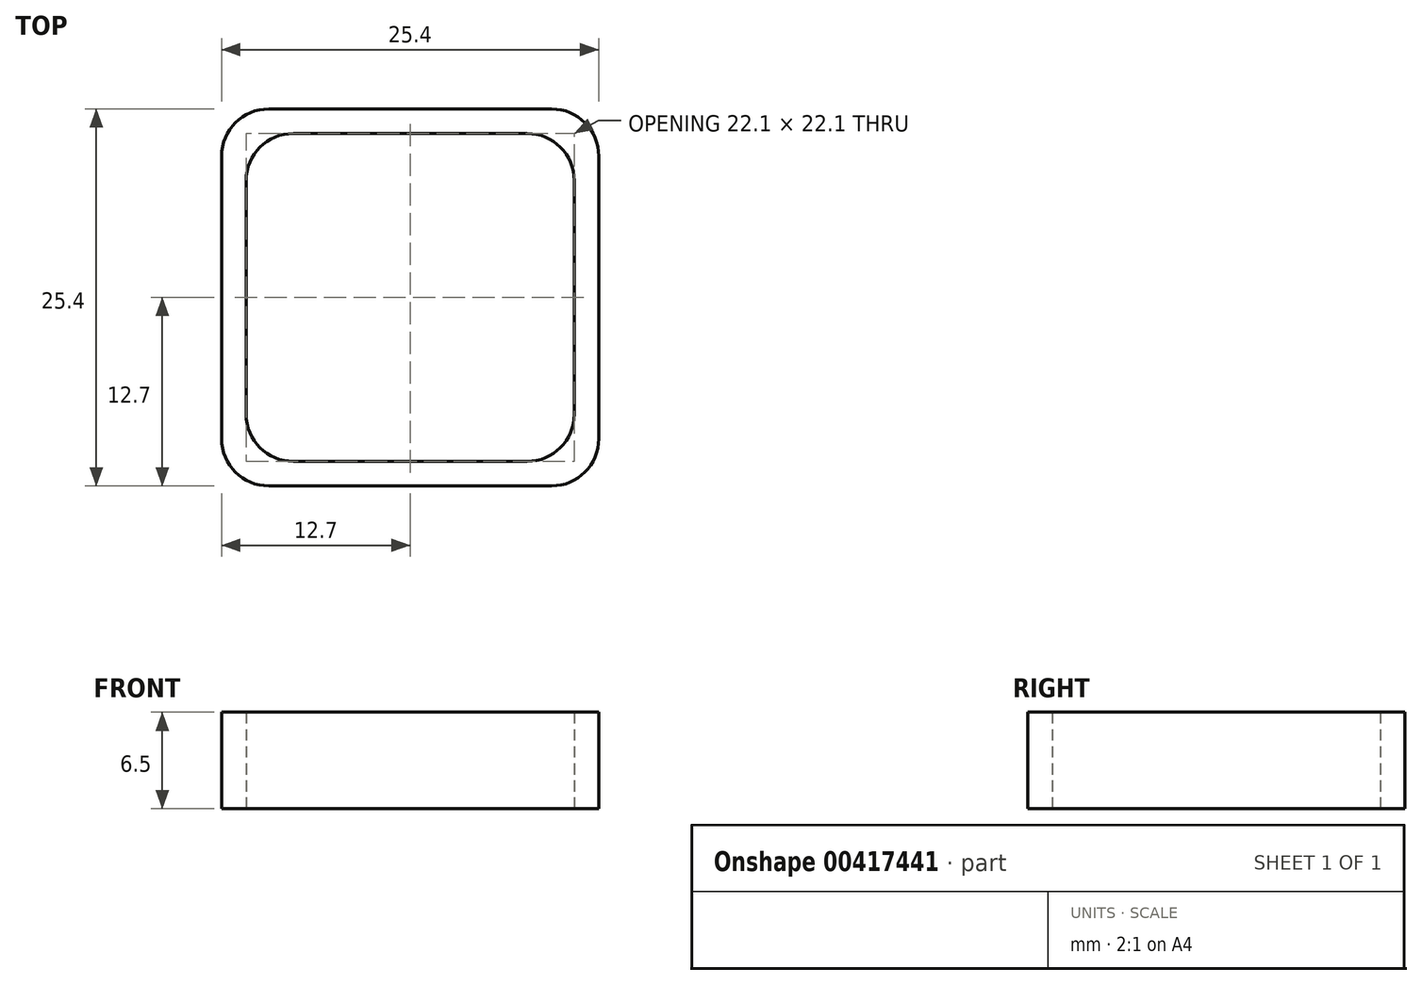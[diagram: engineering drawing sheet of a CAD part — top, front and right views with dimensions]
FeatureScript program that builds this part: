
annotation { "Feature Type Name" : "Feature", "Feature Type Description" : "" }
export const myFeature = defineFeature(function(context is Context, id is Id, definition is map)
    precondition{}
    {
        {
            assignVariable(context, id + "F0", {"name" : "BeamHeight", "anyValue" : 6.5});
        }
        {
            var Q0;
            Q0=qCreatedBy(makeId("Top.planeOp"),FACE);
            var sketch = newSketch(context, id + "F1", { "sketchPlane" : qUnion([Q0])});
            skPoint(sketch, "E0.middle", {"position": v(0, 0) * mm});
            skPoint(sketch, "E1.visualSharp", {"position": v(-12.7, 12.7) * mm});
            skPoint(sketch, "E2.visualSharp", {"position": v(12.7, 12.7) * mm});
            skPoint(sketch, "E3.visualSharp", {"position": v(12.7, -12.7) * mm});
            skPoint(sketch, "E4.visualSharp", {"position": v(-12.7, -12.7) * mm});
            skLineSegment(sketch, "E5.bottom", {"start": v(-7.87, 11.05) * mm, "end": v(7.87, 11.05) * mm});
            skLineSegment(sketch, "E5.top", {"start": v(-7.87, -11.05) * mm, "end": v(7.87, -11.05) * mm});
            skLineSegment(sketch, "E5.left", {"start": v(-11.05, 7.87) * mm, "end": v(-11.05, -7.87) * mm});
            skLineSegment(sketch, "E5.right", {"start": v(11.05, 7.87) * mm, "end": v(11.05, -7.87) * mm});
            skPoint(sketch, "E6.visualSharp", {"position": v(-11.05, 11.05) * mm});
            skArc(sketch, "E6.filletArc", {"start": v(-7.87, 11.05) * mm, "mid": v(-10.12, 10.12) * mm, "end": v(-11.05, 7.87) * mm});
            skPoint(sketch, "E7.visualSharp", {"position": v(11.05, 11.05) * mm});
            skArc(sketch, "E7.filletArc", {"start": v(11.05, 7.87) * mm, "mid": v(10.12, 10.12) * mm, "end": v(7.87, 11.05) * mm});
            skPoint(sketch, "E8.visualSharp", {"position": v(11.05, -11.05) * mm});
            skArc(sketch, "E8.filletArc", {"start": v(7.87, -11.05) * mm, "mid": v(10.12, -10.12) * mm, "end": v(11.05, -7.87) * mm});
            skPoint(sketch, "E9.visualSharp", {"position": v(-11.05, -11.05) * mm});
            skArc(sketch, "E9.filletArc", {"start": v(-11.05, -7.87) * mm, "mid": v(-10.12, -10.12) * mm, "end": v(-7.87, -11.05) * mm});
            skLineSegment(sketch, "E10.bottom", {"start": v(-12.7, 12.7) * mm, "end": v(12.7, 12.7) * mm});
            skLineSegment(sketch, "E10.top", {"start": v(-12.7, -12.7) * mm, "end": v(12.7, -12.7) * mm});
            skLineSegment(sketch, "E10.left", {"start": v(-12.7, 12.7) * mm, "end": v(-12.7, -12.7) * mm});
            skLineSegment(sketch, "E10.right", {"start": v(12.7, 12.7) * mm, "end": v(12.7, -12.7) * mm});
            skSolve(sketch);
        }
        {
            var Q0;
            Q0=makeQuery(id+"F1.imprint","IMPRINT",FACE,{"disambiguationData":[TD([[makeQuery(id+"F1.imprint","IMPRINT",EDGE,{"derivedFrom":sQuery(id+"F1.wireOp",EDGE,"E5.bottom")}),1.0]])]});
            extrude(context, id + "F2", {"entities" : qUnion([Q0]), "depth" : (getVariable(context, 'BeamHeight')) * mm});
        }
        {
            var Q0;
            Q0=makeQuery(id+"F2.opExtrude","SWEPT_FACE",FACE,{"disambiguationData":[OSD([sQuery(id+"F1.wireOp",EDGE,"E10.top")])]});
            var sketch = newSketch(context, id + "F3", { "sketchPlane" : qUnion([Q0])});
            skLineSegment(sketch, "E11", {"start": v(-12.7, 0) * mm, "end": v(12.7, 25.4) * mm});
            skLineSegment(sketch, "E12", {"start": v(12.7, 25.4) * mm, "end": v(12.7, 0) * mm});
            skLineSegment(sketch, "E13", {"start": v(12.7, 0) * mm, "end": v(-12.7, 0) * mm});
            skLineSegment(sketch, "E14", {"start": v(-12.7, 165.1) * mm, "end": v(12.7, 139.7) * mm});
            skLineSegment(sketch, "E15", {"start": v(12.7, 139.7) * mm, "end": v(12.7, 165.1) * mm});
            skLineSegment(sketch, "E16", {"start": v(12.7, 165.1) * mm, "end": v(-12.7, 165.1) * mm});
            skSolve(sketch);
        }
        {
            var Q0;
            Q0=makeQuery(id+"F3.imprint","IMPRINT",FACE,{"disambiguationData":[TD([[makeQuery(id+"F3.imprint","IMPRINT",EDGE,{"derivedFrom":sQuery(id+"F3.wireOp",EDGE,"E11")}),-1.0]])]});
            var Q1;
            Q1=makeQuery(id+"F3.imprint","IMPRINT",FACE,{"disambiguationData":[TD([[makeQuery(id+"F3.imprint","IMPRINT",EDGE,{"derivedFrom":sQuery(id+"F3.wireOp",EDGE,"E14")}),1.0]])]});
            extrude(context, id + "F4", {"entities" : qUnion([Q0, Q1]), "operationType" : NewBodyOperationType.REMOVE, "oppositeDirection" : true, "depth" : 25.4 * mm});
        }
        {
            var Q0;
            Q0=makeQuery(id+"F2.opExtrude","SWEPT_EDGE",EDGE,{"disambiguationData":[OSD([sQuery(id+"F1.wireOp",EDGE,"E10.bottom"),sQuery(id+"F1.wireOp",EDGE,"E10.left")])]});
            var Q1;
            Q1=makeQuery(id+"F2.opExtrude","SWEPT_EDGE",EDGE,{"disambiguationData":[OSD([sQuery(id+"F1.wireOp",EDGE,"E10.bottom"),sQuery(id+"F1.wireOp",EDGE,"E10.right")])]});
            var Q2;
            Q2=makeQuery(id+"F2.opExtrude","SWEPT_EDGE",EDGE,{"disambiguationData":[OSD([sQuery(id+"F1.wireOp",EDGE,"E10.top"),sQuery(id+"F1.wireOp",EDGE,"E10.left")])]});
            var Q3;
            Q3=makeQuery(id+"F2.opExtrude","SWEPT_EDGE",EDGE,{"disambiguationData":[OSD([sQuery(id+"F1.wireOp",EDGE,"E10.top"),sQuery(id+"F1.wireOp",EDGE,"E10.right")])]});
            fillet(context, id + "F5", {"entities" : qUnion([Q0, Q1, Q2, Q3]), "radius" : 3.17 * mm, "tangentPropagation" : true, "allowEdgeOverflow" : false});
        }
    });
